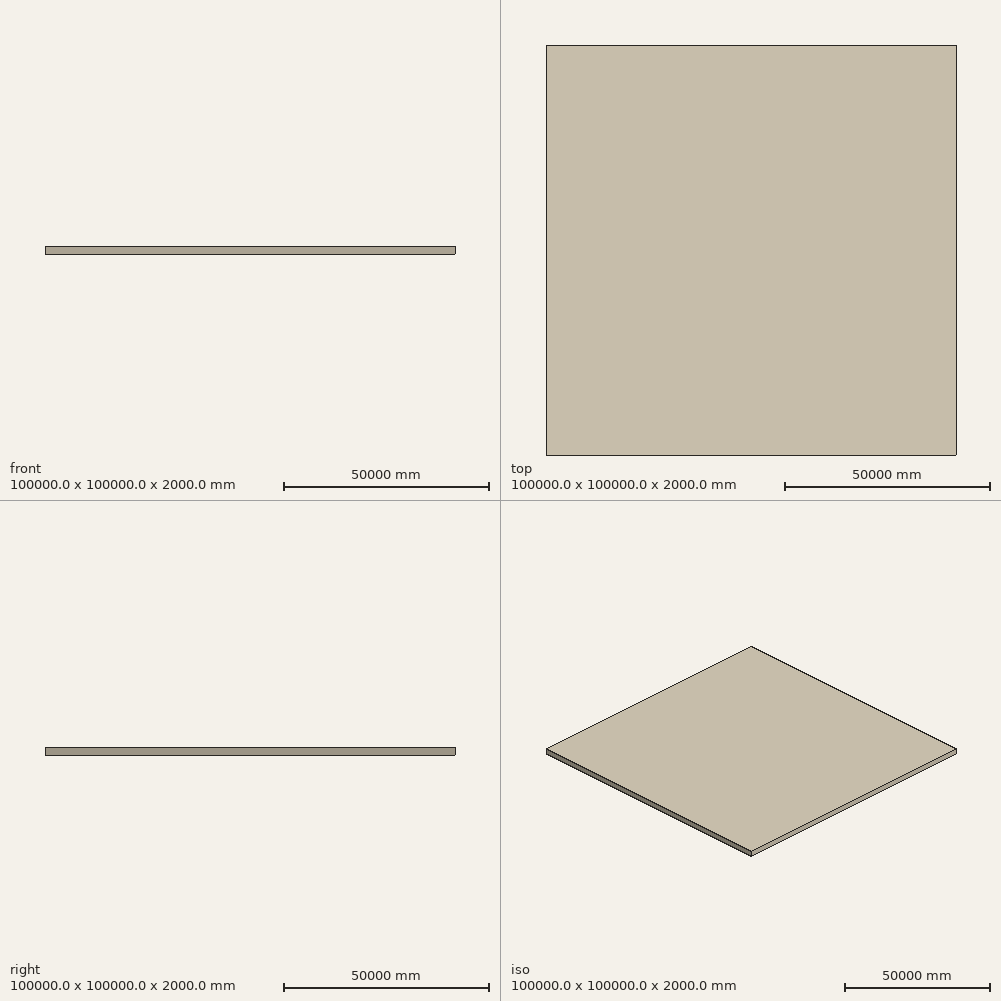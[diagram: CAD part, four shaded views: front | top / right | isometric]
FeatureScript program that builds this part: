
annotation { "Feature Type Name" : "Feature", "Feature Type Description" : "" }
export const myFeature = defineFeature(function(context is Context, id is Id, definition is map)
    precondition{}
    {
        {
            var Q0;
            Q0=qCreatedBy(makeId("Top.planeOp"),FACE);
            var sketch = newSketch(context, id + "F0", { "sketchPlane" : qUnion([Q0])});
            skLineSegment(sketch, "E0.bottom", {"start": v(-50000, 50000) * mm, "end": v(50000, 50000) * mm});
            skLineSegment(sketch, "E0.top", {"start": v(-50000, -50000) * mm, "end": v(50000, -50000) * mm});
            skLineSegment(sketch, "E0.left", {"start": v(-50000, 50000) * mm, "end": v(-50000, -50000) * mm});
            skLineSegment(sketch, "E0.right", {"start": v(50000, 50000) * mm, "end": v(50000, -50000) * mm});
            skPoint(sketch, "E0.middle", {"position": v(0, 0) * mm});
            skSolve(sketch);
        }
        {
            var Q0;
            Q0=qSketchRegion(id+"F0",true);
            extrude(context, id + "F1", {"entities" : qUnion([Q0]), "oppositeDirection" : true, "depth" : 2000 * mm});
        }
    });
